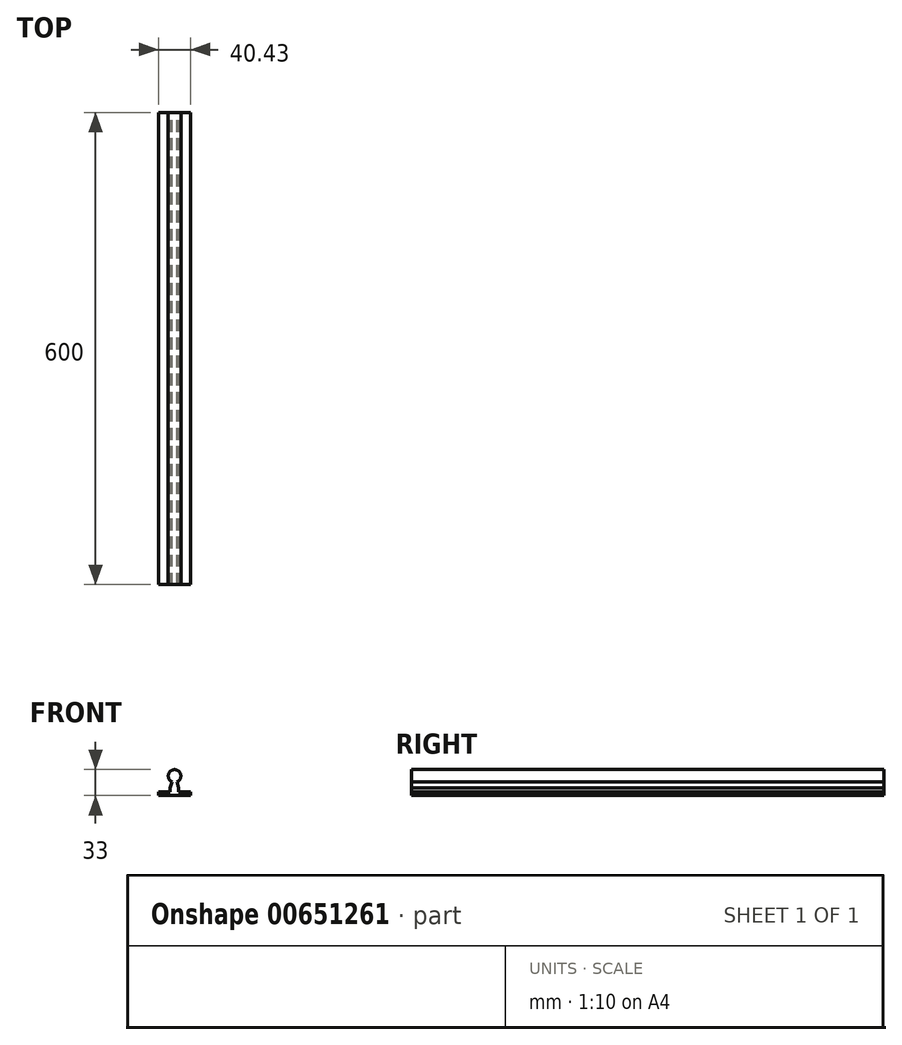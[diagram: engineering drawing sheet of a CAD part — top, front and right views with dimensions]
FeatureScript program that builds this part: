
annotation { "Feature Type Name" : "Feature", "Feature Type Description" : "" }
export const myFeature = defineFeature(function(context is Context, id is Id, definition is map)
    precondition{}
    {
        {
            var Q0;
            Q0=qCreatedBy(makeId("Front.planeOp"),FACE);
            var sketch = newSketch(context, id + "F0", { "sketchPlane" : qUnion([Q0])});
            skArc(sketch, "E0", {"start": v(3.03, -7.4) * mm, "mid": v(0, 8) * mm, "end": v(-3.03, -7.4) * mm});
            skLineSegment(sketch, "E1", {"start": v(0, -25) * mm, "end": v(-20.2, -25) * mm});
            skLineSegment(sketch, "E2", {"start": v(0, -25) * mm, "end": v(20.22, -25) * mm});
            skLineSegment(sketch, "E3", {"start": v(-20.2, -25) * mm, "end": v(-20.2, -20) * mm});
            skLineSegment(sketch, "E4", {"start": v(20.22, -25) * mm, "end": v(20.22, -20) * mm});
            skLineSegment(sketch, "E5", {"start": v(-3.03, -7.4) * mm, "end": v(-5.4, -15.42) * mm});
            skLineSegment(sketch, "E6", {"start": v(-5.4, -15.42) * mm, "end": v(-5.4, -20.15) * mm});
            skLineSegment(sketch, "E7", {"start": v(-5.4, -20.15) * mm, "end": v(-20.2, -20) * mm});
            skLineSegment(sketch, "E8.MirrorCS", {"start": v(3.03, -7.4) * mm, "end": v(5.4, -15.42) * mm});
            skLineSegment(sketch, "E9.MirrorCS", {"start": v(5.4, -15.42) * mm, "end": v(5.4, -20.15) * mm});
            skLineSegment(sketch, "E10.MirrorCS", {"start": v(5.4, -20.15) * mm, "end": v(20.22, -20) * mm});
            skSolve(sketch);
        }
        {
            var Q0;
            Q0=makeQuery(id+"F0.imprint","IMPRINT",FACE,{"disambiguationData":[TD([[makeQuery(id+"F0.imprint","IMPRINT",EDGE,{"derivedFrom":sQuery(id+"F0.wireOp",EDGE,"E0")}),1.0]])]});
            extrude(context, id + "F1", {"entities" : qUnion([Q0]), "depth" : 600 * mm, "offsetDistance" : 25.4 * mm});
        }
    });
